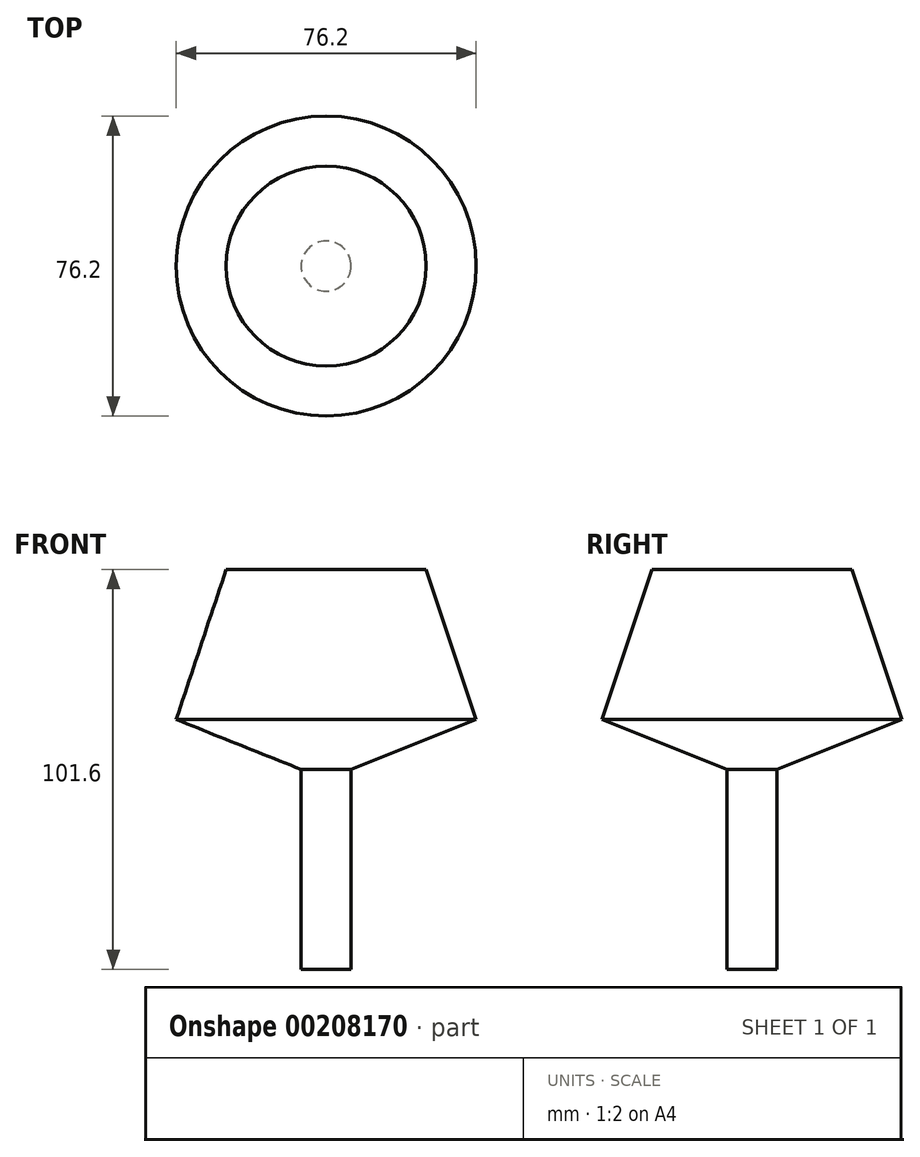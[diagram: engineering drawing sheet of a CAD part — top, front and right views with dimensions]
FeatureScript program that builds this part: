
annotation { "Feature Type Name" : "Feature", "Feature Type Description" : "" }
export const myFeature = defineFeature(function(context is Context, id is Id, definition is map)
    precondition{}
    {
        {
            var Q0;
            Q0=qCreatedBy(makeId("Front.planeOp"),FACE);
            var sketch = newSketch(context, id + "F0", { "sketchPlane" : qUnion([Q0])});
            skLineSegment(sketch, "E0", {"start": v(0, 0) * mm, "end": v(0, 101.6) * mm});
            skLineSegment(sketch, "E1", {"start": v(0, 101.6) * mm, "end": v(25.4, 101.6) * mm});
            skLineSegment(sketch, "E2", {"start": v(25.4, 101.6) * mm, "end": v(38.1, 63.5) * mm});
            skLineSegment(sketch, "E3", {"start": v(38.1, 63.5) * mm, "end": v(6.35, 50.8) * mm});
            skLineSegment(sketch, "E4", {"start": v(6.35, 50.8) * mm, "end": v(6.35, 0) * mm});
            skLineSegment(sketch, "E5", {"start": v(6.35, 0) * mm, "end": v(0, 0) * mm});
            skSolve(sketch);
        }
        {
            var Q0;
            Q0=makeQuery(id+"F0.imprint","IMPRINT",FACE,{"disambiguationData":[TD([[makeQuery(id+"F0.imprint","IMPRINT",EDGE,{"derivedFrom":sQuery(id+"F0.wireOp",EDGE,"E0")}),-1.0]])]});
            var Q1;
            Q1=sQuery(id+"F0.wireOp",EDGE,"E0");
            revolve(context, id + "F1", {"entities" : qUnion([Q0]), "axis" : qUnion([Q1]), "revolveType" : RevolveType.FULL});
        }
    });
